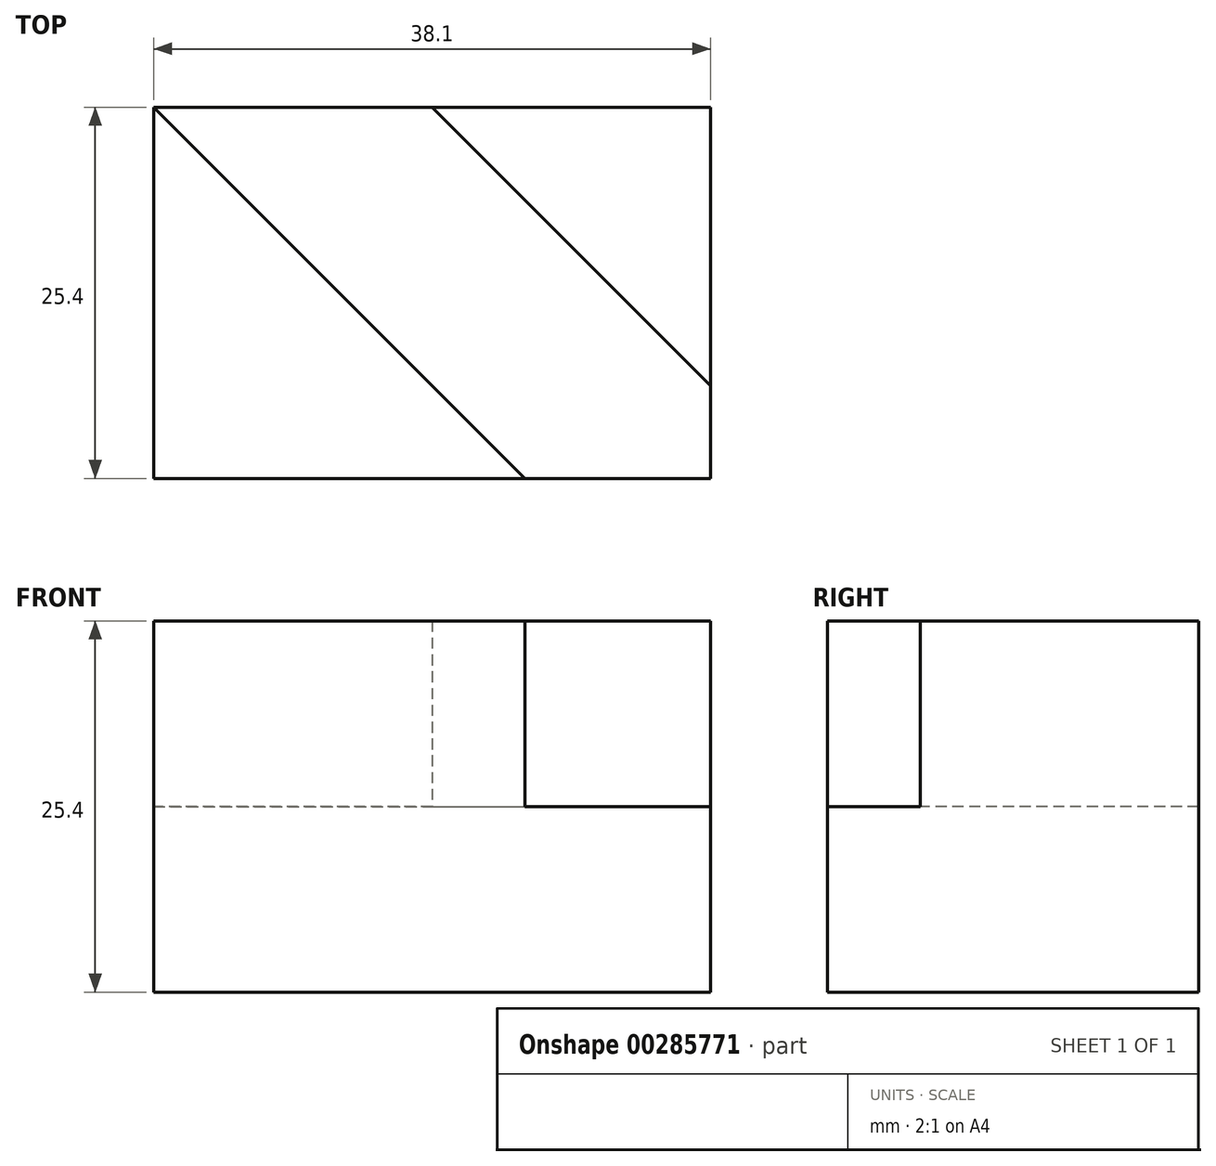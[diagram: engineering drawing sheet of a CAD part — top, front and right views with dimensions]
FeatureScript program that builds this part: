
annotation { "Feature Type Name" : "Feature", "Feature Type Description" : "" }
export const myFeature = defineFeature(function(context is Context, id is Id, definition is map)
    precondition{}
    {
        {
            var Q0;
            Q0=qCreatedBy(makeId("Top.planeOp"),FACE);
            var sketch = newSketch(context, id + "F0", { "sketchPlane" : qUnion([Q0])});
            skLineSegment(sketch, "E0", {"start": v(0, 0) * mm, "end": v(38.1, 0) * mm});
            skLineSegment(sketch, "E1", {"start": v(38.1, 0) * mm, "end": v(38.1, 25.4) * mm});
            skLineSegment(sketch, "E2", {"start": v(38.1, 25.4) * mm, "end": v(0, 25.4) * mm});
            skLineSegment(sketch, "E3", {"start": v(0, 25.4) * mm, "end": v(0, 0) * mm});
            skLineSegment(sketch, "E4", {"start": v(0, 25.4) * mm, "end": v(25.4, 0) * mm});
            skLineSegment(sketch, "E5", {"start": v(19.05, 25.4) * mm, "end": v(38.1, 6.35) * mm});
            skSolve(sketch);
        }
        {
            var Q0;
            {var subQ3=sQuery(id+"F0.wireOp",EDGE,"E5");Q0=makeQuery(id+"F0.imprint","IMPRINT",FACE,{"disambiguationData":[TD([[makeQuery(id+"F0.imprint","IMPRINT",EDGE,{"derivedFrom":subQ3}),1.0]])]});}
            var Q1;
            {var subQ0=sQuery(id+"F0.wireOp",EDGE,"E3");Q1=makeQuery(id+"F0.imprint","IMPRINT",FACE,{"disambiguationData":[TD([[makeQuery(id+"F0.imprint","IMPRINT",EDGE,{"derivedFrom":subQ0}),1.0]])]});}
            extrude(context, id + "F1", {"entities" : qUnion([Q0, Q1]), "depth" : 25.4 * mm});
        }
        {
            var Q0;
            {var subQ0=sQuery(id+"F0.wireOp",EDGE,"E4");Q0=makeQuery(id+"F0.imprint","IMPRINT",FACE,{"disambiguationData":[TD([[makeQuery(id+"F0.imprint","IMPRINT",EDGE,{"derivedFrom":subQ0}),1.0]])]});}
            extrude(context, id + "F2", {"entities" : qUnion([Q0]), "operationType" : NewBodyOperationType.ADD, "depth" : 12.7 * mm});
        }
    });
